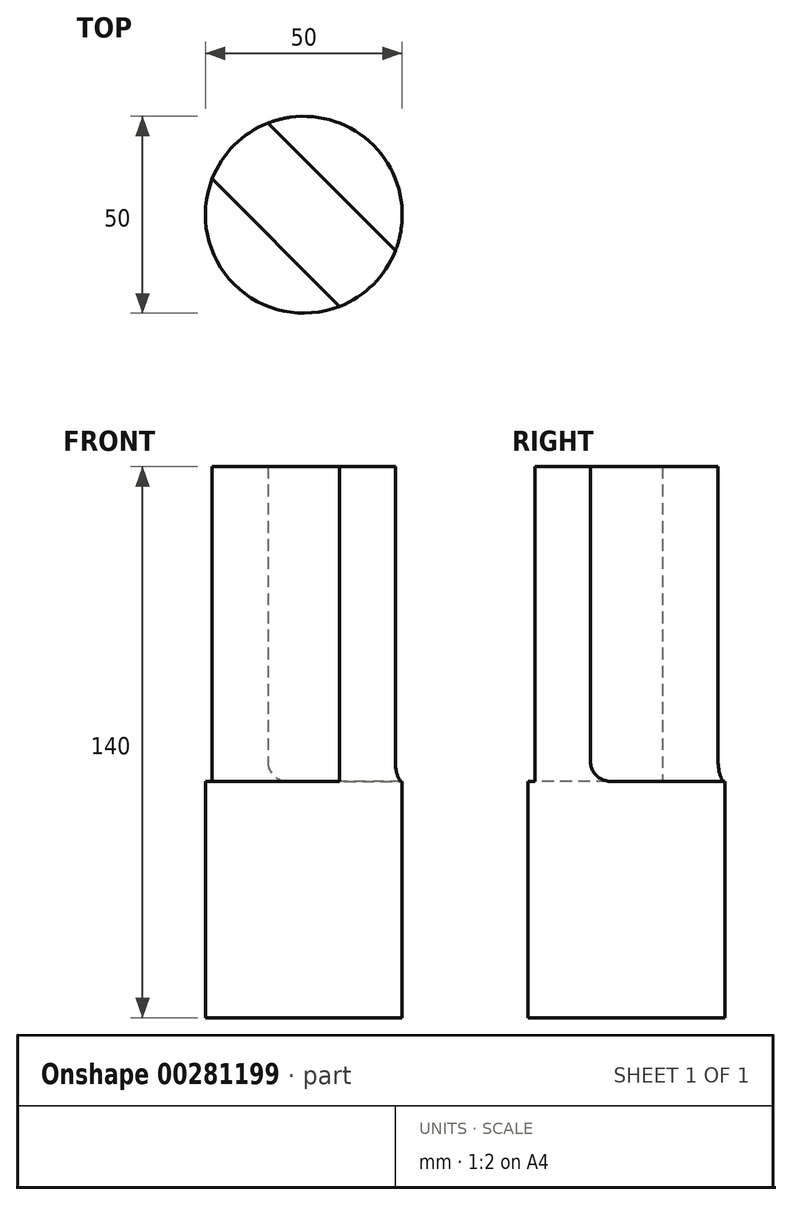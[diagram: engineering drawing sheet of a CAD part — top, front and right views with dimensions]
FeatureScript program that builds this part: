
annotation { "Feature Type Name" : "Feature", "Feature Type Description" : "" }
export const myFeature = defineFeature(function(context is Context, id is Id, definition is map)
    precondition{}
    {
        {
            var Q0;
            Q0=qCreatedBy(makeId("Top.planeOp"),FACE);
            var sketch = newSketch(context, id + "F0", { "sketchPlane" : qUnion([Q0])});
            skCircle(sketch, "E0", {"center": v(0, 0) * mm, "radius": 25 * mm});
            skSolve(sketch);
        }
        {
            var Q0;
            Q0=makeQuery(id+"F0.imprint","IMPRINT",FACE,{"disambiguationData":[TD([[makeQuery(id+"F0.imprint","IMPRINT",EDGE,{"derivedFrom":sQuery(id+"F0.wireOp",EDGE,"E0")}),1.0]])]});
            extrude(context, id + "F1", {"entities" : qUnion([Q0]), "depth" : 60 * mm});
        }
        {
            var Q0;
            Q0=makeQuery(id+"F1.opExtrude","CAP_FACE",FACE,{"disambiguationData":[OSD([sQuery(id+"F0.wireOp",EDGE,"E0")])],"isStart":false});
            var sketch = newSketch(context, id + "F2", { "sketchPlane" : qUnion([Q0])});
            skLineSegment(sketch, "E1", {"start": v(27.82, -27.83) * mm, "end": v(-37.55, 37.57) * mm});
            skPoint(sketch, "E2.orphan", {"position": v(0, 0) * mm});
            skLineSegment(sketch, "E3", {"start": v(-38.58, 24.45) * mm, "end": v(17.95, -32.1) * mm});
            skLineSegment(sketch, "E4", {"start": v(-24.1, 38.26) * mm, "end": v(31.23, -17.1) * mm});
            skCircle(sketch, "E5.0", {"center": v(0, 0) * mm, "radius": 25 * mm});
            skSolve(sketch);
        }
        {
            var Q0;
            {var subQ0=sQuery(id+"F2.wireOp",EDGE,"E5.0");var subQ1=sQuery(id+"F2.wireOp",EDGE,"E1");var subQ2=makeQuery(id+"F2.imprint","INTERSECT",VERTEX,{"disambiguationData":[OD(0.0)],"derivedFrom":[subQ1,subQ0]});Q0=makeQuery(id+"F2.imprint","IMPRINT",FACE,{"disambiguationData":[TD([[makeQuery(id+"F2.imprint","IMPRINT",EDGE,{"disambiguationData":[TD([[subQ2,1.0]])],"derivedFrom":subQ1}),1.0]])]});}
            var Q1;
            {var subQ0=sQuery(id+"F2.wireOp",EDGE,"E5.0");var subQ1=sQuery(id+"F2.wireOp",EDGE,"E1");var subQ2=makeQuery(id+"F2.imprint","INTERSECT",VERTEX,{"disambiguationData":[OD(0.0)],"derivedFrom":[subQ1,subQ0]});Q1=makeQuery(id+"F2.imprint","IMPRINT",FACE,{"disambiguationData":[TD([[makeQuery(id+"F2.imprint","IMPRINT",EDGE,{"disambiguationData":[TD([[subQ2,1.0]])],"derivedFrom":subQ1}),-1.0]])]});}
            extrude(context, id + "F3", {"entities" : qUnion([Q0, Q1]), "operationType" : NewBodyOperationType.ADD, "depth" : 80 * mm});
        }
        {
            var Q0;
            Q0=makeQuery(id+"F3.opExtrude","CAP_EDGE",EDGE,{"disambiguationData":[OSD([sQuery(id+"F2.wireOp",EDGE,"E4")])],"isStart":true});
            var Q1;
            Q1=makeQuery(id+"F3.opExtrude","CAP_EDGE",EDGE,{"disambiguationData":[OSD([sQuery(id+"F2.wireOp",EDGE,"E3")])],"isStart":true});
            fillet(context, id + "F4", {"entities" : qUnion([Q0, Q1]), "radius" : 5 * mm, "tangentPropagation" : true, "allowEdgeOverflow" : false});
        }
    });
